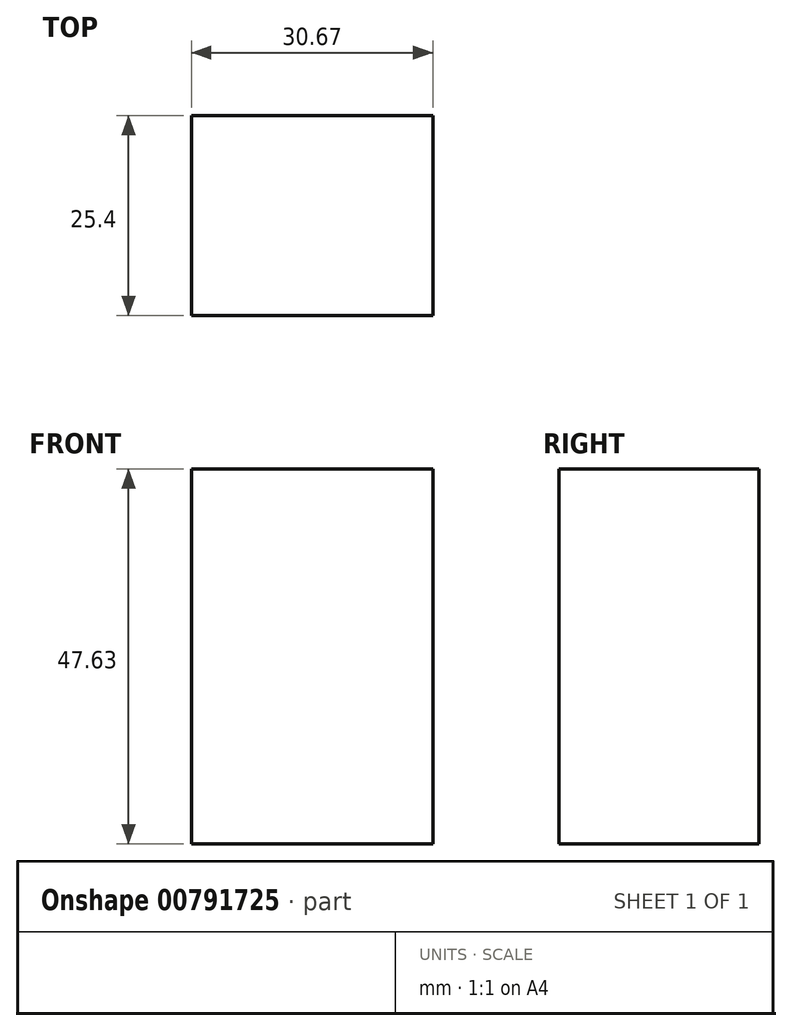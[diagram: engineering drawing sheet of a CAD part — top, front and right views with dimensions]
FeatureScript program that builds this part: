
annotation { "Feature Type Name" : "Feature", "Feature Type Description" : "" }
export const myFeature = defineFeature(function(context is Context, id is Id, definition is map)
    precondition{}
    {
        {
            var Q0;
            Q0=qCreatedBy(makeId("Front.planeOp"),FACE);
            var sketch = newSketch(context, id + "F0", { "sketchPlane" : qUnion([Q0])});
            skLineSegment(sketch, "E0.bottom", {"start": v(-135.31, 59.66) * mm, "end": v(-104.64, 59.66) * mm});
            skLineSegment(sketch, "E0.top", {"start": v(-135.31, 12.03) * mm, "end": v(-104.64, 12.03) * mm});
            skLineSegment(sketch, "E0.left", {"start": v(-135.31, 59.66) * mm, "end": v(-135.31, 12.03) * mm});
            skLineSegment(sketch, "E0.right", {"start": v(-104.64, 59.66) * mm, "end": v(-104.64, 12.03) * mm});
            skSolve(sketch);
        }
        {
            var Q0;
            Q0=makeQuery(id+"F0.imprint","IMPRINT",FACE,{"disambiguationData":[TD([[makeQuery(id+"F0.imprint","IMPRINT",EDGE,{"derivedFrom":sQuery(id+"F0.wireOp",EDGE,"E0.bottom")}),-1.0]])]});
            extrude(context, id + "F1", {"entities" : qUnion([Q0]), "depth" : 25.4 * mm, "offsetDistance" : 25.4 * mm});
        }
    });
